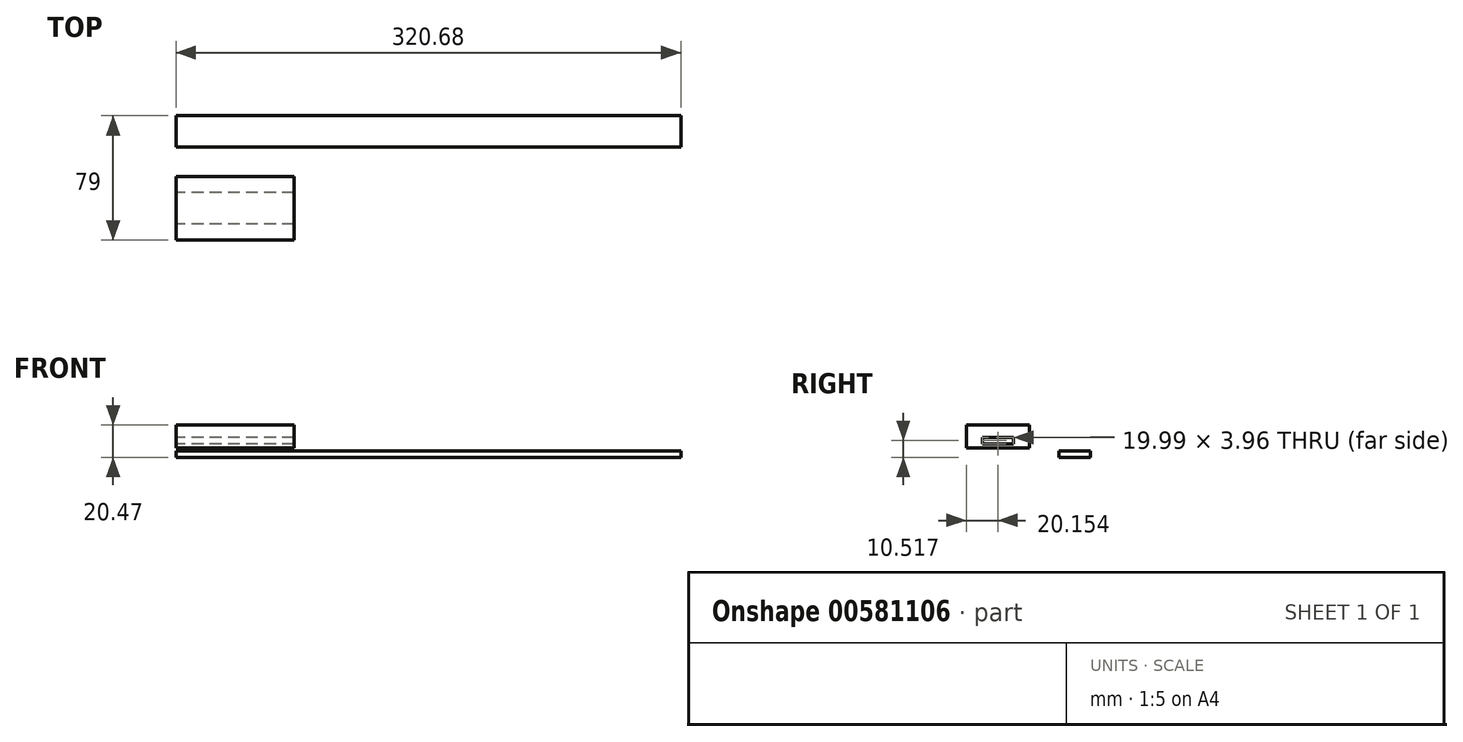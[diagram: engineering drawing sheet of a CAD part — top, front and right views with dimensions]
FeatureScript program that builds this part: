
annotation { "Feature Type Name" : "Feature", "Feature Type Description" : "" }
export const myFeature = defineFeature(function(context is Context, id is Id, definition is map)
    precondition{}
    {
        {
            var Q0;
            Q0=qCreatedBy(makeId("Right.planeOp"),FACE);
            var sketch = newSketch(context, id + "F0", { "sketchPlane" : qUnion([Q0])});
            skLineSegment(sketch, "E0.bottom", {"start": v(0, 0) * mm, "end": v(20.02, 0) * mm});
            skLineSegment(sketch, "E0.top", {"start": v(0, 3.96) * mm, "end": v(20.02, 3.96) * mm});
            skLineSegment(sketch, "E0.left", {"start": v(0, 0) * mm, "end": v(0, 3.96) * mm});
            skLineSegment(sketch, "E0.right", {"start": v(20.02, 0) * mm, "end": v(20.02, 3.96) * mm});
            skSolve(sketch);
        }
        {
            var Q0;
            Q0=makeQuery(id+"F0.imprint","IMPRINT",FACE,{"disambiguationData":[TD([[makeQuery(id+"F0.imprint","IMPRINT",EDGE,{"derivedFrom":sQuery(id+"F0.wireOp",EDGE,"E0.bottom")}),1.0]])]});
            extrude(context, id + "F1", {"entities" : qUnion([Q0]), "depth" : 320.67 * mm, "offsetDistance" : 25.4 * mm});
        }
        {
            var Q0;
            Q0=qCreatedBy(makeId("Right.planeOp"),FACE);
            var sketch = newSketch(context, id + "F2", { "sketchPlane" : qUnion([Q0])});
            skLineSegment(sketch, "E1.bottom", {"start": v(-48.82, 8.54) * mm, "end": v(-28.83, 8.54) * mm});
            skLineSegment(sketch, "E1.top", {"start": v(-48.82, 12.5) * mm, "end": v(-28.83, 12.5) * mm});
            skLineSegment(sketch, "E1.left", {"start": v(-48.82, 8.54) * mm, "end": v(-48.82, 12.5) * mm});
            skLineSegment(sketch, "E1.right", {"start": v(-28.83, 8.54) * mm, "end": v(-28.83, 12.5) * mm});
            skLineSegment(sketch, "E2.bottom", {"start": v(-58.98, 6) * mm, "end": v(-18.72, 6) * mm});
            skLineSegment(sketch, "E2.top", {"start": v(-58.98, 20.47) * mm, "end": v(-18.72, 20.47) * mm});
            skLineSegment(sketch, "E2.left", {"start": v(-58.98, 6) * mm, "end": v(-58.98, 20.47) * mm});
            skLineSegment(sketch, "E2.right", {"start": v(-18.72, 6) * mm, "end": v(-18.72, 20.47) * mm});
            skSolve(sketch);
        }
        {
            var Q0;
            Q0=makeQuery(id+"F2.imprint","IMPRINT",FACE,{"disambiguationData":[TD([[makeQuery(id+"F2.imprint","IMPRINT",EDGE,{"derivedFrom":sQuery(id+"F2.wireOp",EDGE,"E1.bottom")}),-1.0]])]});
            extrude(context, id + "F3", {"entities" : qUnion([Q0]), "depth" : 74.93 * mm, "offsetDistance" : 25.4 * mm});
        }
    });
